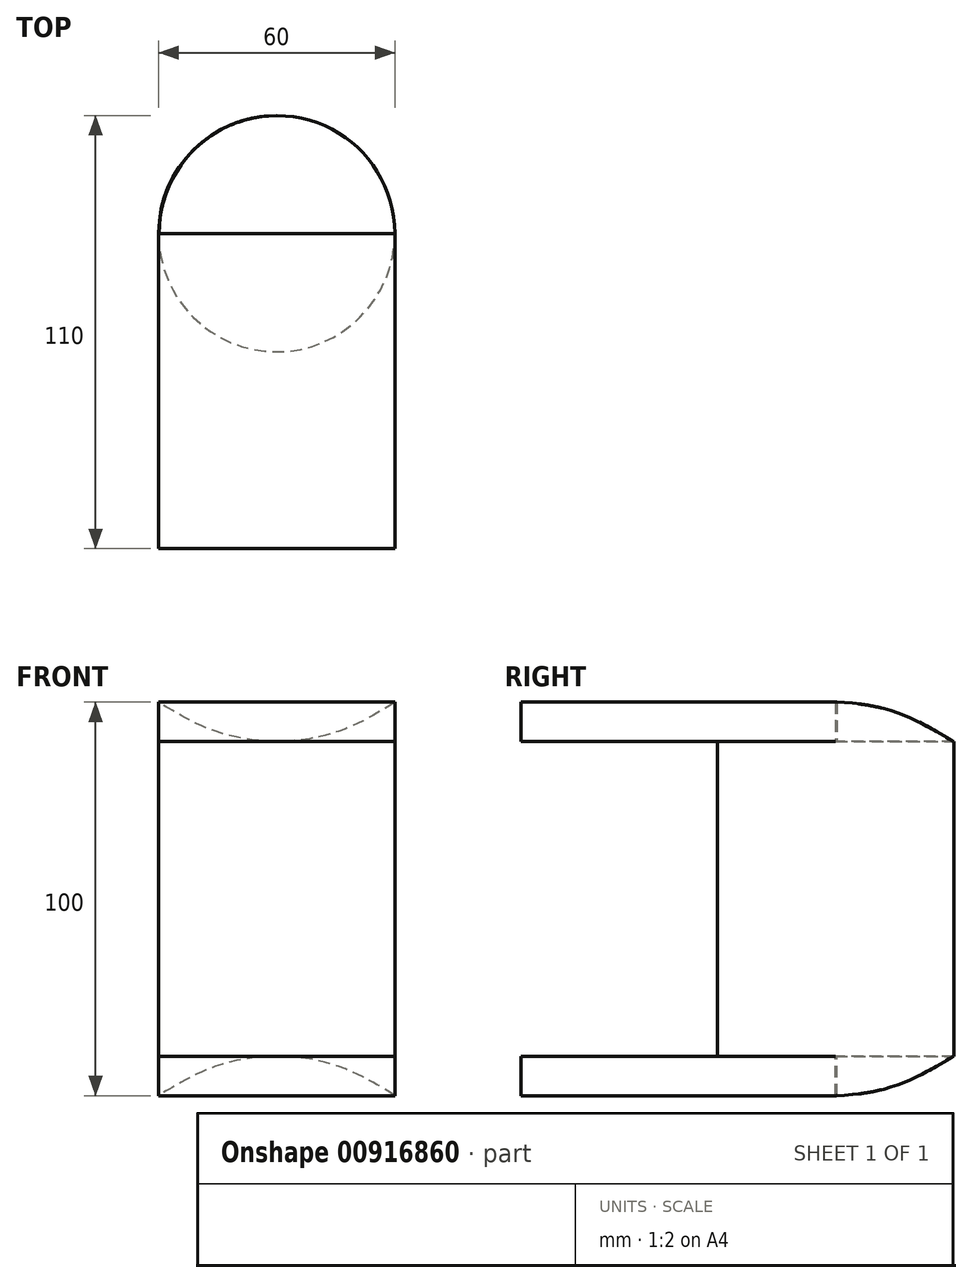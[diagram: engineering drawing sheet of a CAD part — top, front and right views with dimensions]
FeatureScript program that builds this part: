
annotation { "Feature Type Name" : "Feature", "Feature Type Description" : "" }
export const myFeature = defineFeature(function(context is Context, id is Id, definition is map)
    precondition{}
    {
        {
            var Q0;
            Q0=qCreatedBy(makeId("Top.planeOp"),FACE);
            var sketch = newSketch(context, id + "F0", { "sketchPlane" : qUnion([Q0])});
            skCircle(sketch, "E0", {"center": v(0, 0) * mm, "radius": 30 * mm});
            skSolve(sketch);
        }
        {
            var Q0;
            Q0 = qSketchRegion(id + "F0", true);
            extrude(context, id + "F1", {"entities" : qUnion([Q0]), "depth" : 25 * mm, "offsetDistance" : 25 * mm});
        }
        {
            var Q0;
            Q0=makeQuery(id+"F1.opExtrude","CAP_FACE",FACE,{"disambiguationData":[OSD([sQuery(id+"F0.wireOp",EDGE,"E0")])],"isStart":false});
            var sketch = newSketch(context, id + "F2", { "sketchPlane" : qUnion([Q0])});
            skArc(sketch, "E1", {"start": v(30, 0) * mm, "mid": v(0, 30) * mm, "end": v(-30, 0) * mm});
            skLineSegment(sketch, "E2.bottom", {"start": v(-30, 0) * mm, "end": v(30, 0) * mm});
            skLineSegment(sketch, "E2.top", {"start": v(-30, -80) * mm, "end": v(30, -80) * mm});
            skLineSegment(sketch, "E2.left", {"start": v(-30, 0) * mm, "end": v(-30, -80) * mm});
            skLineSegment(sketch, "E2.right", {"start": v(30, 0) * mm, "end": v(30, -80) * mm});
            skSolve(sketch);
        }
        {
            var Q0;
            Q0=makeQuery(id+"F2.imprint","IMPRINT",FACE,{"disambiguationData":[TD([[makeQuery(id+"F2.imprint","IMPRINT",EDGE,{"derivedFrom":sQuery(id+"F2.wireOp",EDGE,"E2.top")}),1.0]])]});
            var Q1;
            {var subQ0=sQuery(id+"F2.wireOp",EDGE,"E2.bottom");Q1=makeQuery(id+"F2.imprint","IMPRINT",FACE,{"disambiguationData":[TD([[makeQuery(id+"F2.imprint","IMPRINT",EDGE,{"derivedFrom":subQ0}),-1.0]])]});}
            extrude(context, id + "F3", {"entities" : qUnion([Q0, Q1]), "operationType" : NewBodyOperationType.ADD, "depth" : 10 * mm, "offsetDistance" : 25 * mm});
        }
        {
            var Q0;
            Q0=qCreatedBy(makeId("Right.planeOp"),FACE);
            var sketch = newSketch(context, id + "F4", { "sketchPlane" : qUnion([Q0])});
            skFitSpline(sketch, "E3", {"points": [v(0, 35) * mm, v(5.15, 34.63) * mm, v(15.97, 32.18) * mm, v(30, 25) * mm], "startDerivative": vector(19.79, -1.22) * mm, "endDerivative": vector(33.8, -20.02) * mm});
            skLineSegment(sketch, "E4", {"start": v(0, 35) * mm, "end": v(0, 25) * mm});
            skLineSegment(sketch, "E5", {"start": v(0, 25) * mm, "end": v(30, 25) * mm});
            skSolve(sketch);
        }
        {
            var Q0;
            Q0 = qSketchRegion(id + "F4", true);
            extrude(context, id + "F5", {"entities" : qUnion([Q0]), "operationType" : NewBodyOperationType.ADD, "endBound" : BoundingType.SYMMETRIC, "depth" : 60 * mm, "offsetDistance" : 25 * mm});
        }
        {
            var Q0;
            {var subQ1=sQuery(id+"F2.wireOp",EDGE,"E2.right");var subQ2=sQuery(id+"F4.wireOp",EDGE,"E5");var subQ3=makeQuery(id+"F5.opExtrude","SWEPT_FACE",FACE,{"disambiguationData":[OSD([subQ2])]});Q0=makeQuery(id+"F5.boolean.opBoolean","SPLIT",FACE,{"disambiguationData":[TD([makeQuery(id+"F3.opExtrude","SWEPT_FACE",FACE,{"disambiguationData":[OSD([subQ1])]})])],"derivedFrom":subQ3});}
            var sketch = newSketch(context, id + "F6", { "sketchPlane" : qUnion([Q0])});
            skArc(sketch, "E6", {"start": v(-29.86, 0) * mm, "mid": v(0.07, -30) * mm, "end": v(30, 0) * mm});
            skLineSegment(sketch, "E7", {"start": v(-29.86, 0) * mm, "end": v(-41.98, -29.05) * mm});
            skLineSegment(sketch, "E8", {"start": v(-41.98, -29.05) * mm, "end": v(37.65, -40.4) * mm});
            skLineSegment(sketch, "E9", {"start": v(37.65, -40.4) * mm, "end": v(30, 0) * mm});
            skSolve(sketch);
        }
        {
            var Q0;
            Q0 = qSketchRegion(id + "F6", true);
            extrude(context, id + "F7", {"entities" : qUnion([Q0]), "operationType" : NewBodyOperationType.REMOVE, "oppositeDirection" : true, "depth" : 25 * mm, "offsetDistance" : 25 * mm});
        }
        {
            var Q0;
            Q0=makeQuery(id+"F1.opExtrude","CAP_FACE",FACE,{"disambiguationData":[OSD([sQuery(id+"F0.wireOp",EDGE,"E0")])],"isStart":true});
            var sketch = newSketch(context, id + "F8", { "sketchPlane" : qUnion([Q0])});
            skCircle(sketch, "E10", {"center": v(0, 0) * mm, "radius": 30 * mm});
            skSolve(sketch);
        }
        {
            var Q0;
            Q0 = qSketchRegion(id + "F8", true);
            extrude(context, id + "F9", {"entities" : qUnion([Q0]), "operationType" : NewBodyOperationType.ADD, "depth" : 15 * mm, "offsetDistance" : 25 * mm});
        }
        {
            var Q0;
            Q0=makeQuery(id+"F1.opExtrude","SWEPT_BODY",BODY,{"disambiguationData":[OSD([sQuery(id+"F0.wireOp",EDGE,"E0")])]});
            var Q1;
            Q1=makeQuery(id+"F9.opExtrude","CAP_FACE",FACE,{"disambiguationData":[OSD([sQuery(id+"F8.wireOp",EDGE,"E10")])],"isStart":false});
            mirror(context, id + "F10", {"operationType" : NewBodyOperationType.ADD, "entities" : qUnion([Q0]), "mirrorPlane" : qUnion([Q1])});
        }
    });
